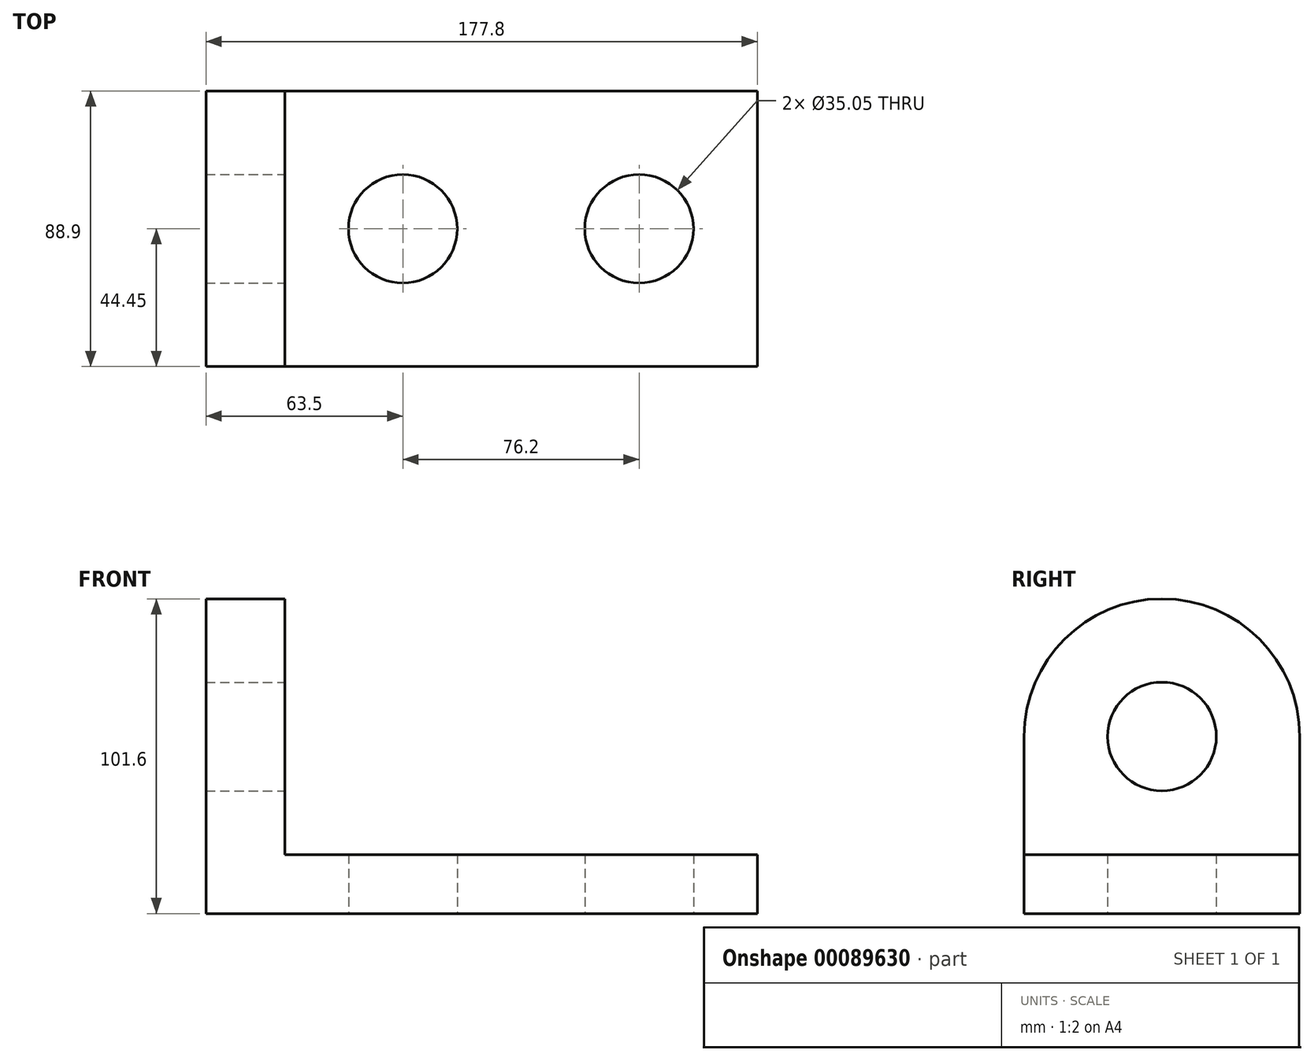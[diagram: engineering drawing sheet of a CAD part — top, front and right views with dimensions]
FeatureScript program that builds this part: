
annotation { "Feature Type Name" : "Feature", "Feature Type Description" : "" }
export const myFeature = defineFeature(function(context is Context, id is Id, definition is map)
    precondition{}
    {
        {
            var Q0;
            Q0=qCreatedBy(makeId("Top.planeOp"),FACE);
            var sketch = newSketch(context, id + "F0", { "sketchPlane" : qUnion([Q0])});
            skLineSegment(sketch, "E0.bottom", {"start": v(0, 0) * mm, "end": v(152.4, 0) * mm});
            skLineSegment(sketch, "E0.top", {"start": v(0, 88.9) * mm, "end": v(152.4, 88.9) * mm});
            skLineSegment(sketch, "E0.left", {"start": v(0, 0) * mm, "end": v(0, 88.9) * mm});
            skLineSegment(sketch, "E0.right", {"start": v(152.4, 0) * mm, "end": v(152.4, 88.9) * mm});
            skLineSegment(sketch, "E1", {"start": v(152.4, 44.45) * mm, "end": v(114.3, 44.45) * mm});
            skLineSegment(sketch, "E2", {"start": v(114.3, 44.45) * mm, "end": v(38.1, 44.45) * mm});
            skCircle(sketch, "E3", {"center": v(114.3, 44.45) * mm, "radius": 17.53 * mm});
            skCircle(sketch, "E4", {"center": v(38.1, 44.45) * mm, "radius": 26.9 * mm});
            skCircle(sketch, "E5", {"center": v(38.1, 44.45) * mm, "radius": 17.53 * mm});
            skSolve(sketch);
        }
        {
            var Q0;
            {var subQ1=sQuery(id+"F0.wireOp",EDGE,"E0.bottom");Q0=makeQuery(id+"F0.imprint","IMPRINT",FACE,{"disambiguationData":[TD([[makeQuery(id+"F0.imprint","IMPRINT",EDGE,{"derivedFrom":subQ1}),1.0]])]});}
            var Q1;
            Q1=makeQuery(id+"F0.imprint","IMPRINT",FACE,{"disambiguationData":[TD([[makeQuery(id+"F0.imprint","IMPRINT",EDGE,{"derivedFrom":sQuery(id+"F0.wireOp",EDGE,"E4")}),1.0]])]});
            extrude(context, id + "F1", {"entities" : qUnion([Q0, Q1]), "depth" : 19.05 * mm});
        }
        {
            var Q0;
            Q0=makeQuery(id+"F1.opExtrude","SWEPT_FACE",FACE,{"disambiguationData":[OSD([sQuery(id+"F0.wireOp",EDGE,"E0.left")])]});
            var sketch = newSketch(context, id + "F2", { "sketchPlane" : qUnion([Q0])});
            skLineSegment(sketch, "E6.bottom", {"start": v(0, 0) * mm, "end": v(-88.9, 0) * mm});
            skLineSegment(sketch, "E6.top", {"start": v(0, 57.15) * mm, "end": v(-88.9, 57.15) * mm});
            skLineSegment(sketch, "E6.left", {"start": v(0, 0) * mm, "end": v(0, 57.15) * mm});
            skLineSegment(sketch, "E6.right", {"start": v(-88.9, 0) * mm, "end": v(-88.9, 57.15) * mm});
            skCircle(sketch, "E7", {"center": v(-44.45, 57.15) * mm, "radius": 44.45 * mm});
            skCircle(sketch, "E8", {"center": v(-44.45, 57.15) * mm, "radius": 17.53 * mm});
            skSolve(sketch);
        }
        {
            var Q0;
            {var subQ1=sQuery(id+"F2.wireOp",EDGE,"E6.top");var subQ3=sQuery(id+"F2.wireOp",EDGE,"E8");var subQ4=makeQuery(id+"F2.imprint","INTERSECT",VERTEX,{"disambiguationData":[OD(0.0)],"derivedFrom":[subQ1,subQ3]});Q0=makeQuery(id+"F2.imprint","IMPRINT",FACE,{"disambiguationData":[TD([[makeQuery(id+"F2.imprint","IMPRINT",EDGE,{"disambiguationData":[TD([[subQ4,-1.0]])],"derivedFrom":subQ3}),-1.0]])]});}
            var Q1;
            {var subQ0=sQuery(id+"F2.wireOp",EDGE,"E6.left");var subQ1=makeQuery(id+"F1.opExtrude","CAP_EDGE",EDGE,{"disambiguationData":[OSD([sQuery(id+"F0.wireOp",EDGE,"E0.left")])],"isStart":false});var subQ2=makeQuery(id+"F2.imprint","INTERSECT",VERTEX,{"derivedFrom":[subQ1,subQ0]});Q1=makeQuery(id+"F2.imprint","IMPRINT",FACE,{"disambiguationData":[TD([[makeQuery(id+"F2.imprint","IMPRINT",EDGE,{"disambiguationData":[TD([[subQ2,-1.0]])],"derivedFrom":subQ1}),-1.0]])]});}
            var Q2;
            {var subQ0=sQuery(id+"F2.wireOp",EDGE,"E6.right");var subQ1=makeQuery(id+"F1.opExtrude","CAP_EDGE",EDGE,{"disambiguationData":[OSD([sQuery(id+"F0.wireOp",EDGE,"E0.left")])],"isStart":false});var subQ2=makeQuery(id+"F2.imprint","INTERSECT",VERTEX,{"derivedFrom":[subQ1,subQ0]});Q2=makeQuery(id+"F2.imprint","IMPRINT",FACE,{"disambiguationData":[TD([[makeQuery(id+"F2.imprint","IMPRINT",EDGE,{"disambiguationData":[TD([[subQ2,1.0]])],"derivedFrom":subQ1}),-1.0]])]});}
            var Q3;
            {var subQ0=sQuery(id+"F2.wireOp",EDGE,"E7");var subQ1=makeQuery(id+"F1.opExtrude","CAP_EDGE",EDGE,{"disambiguationData":[OSD([sQuery(id+"F0.wireOp",EDGE,"E0.left")])],"isStart":false});var subQ2=makeQuery(id+"F2.imprint","INTERSECT",VERTEX,{"disambiguationData":[OD(0.0)],"derivedFrom":[subQ1,subQ0]});Q3=makeQuery(id+"F2.imprint","IMPRINT",FACE,{"disambiguationData":[TD([[makeQuery(id+"F2.imprint","IMPRINT",EDGE,{"disambiguationData":[TD([[subQ2,-1.0]])],"derivedFrom":subQ0}),1.0]])]});}
            var Q4;
            {var subQ1=sQuery(id+"F2.wireOp",EDGE,"E6.bottom");Q4=makeQuery(id+"F2.imprint","IMPRINT",FACE,{"disambiguationData":[TD([[makeQuery(id+"F2.imprint","IMPRINT",EDGE,{"derivedFrom":subQ1}),-1.0]])]});}
            var Q5;
            {var subQ1=sQuery(id+"F2.wireOp",EDGE,"E6.top");var subQ7=sQuery(id+"F2.wireOp",EDGE,"E8");var subQ9=makeQuery(id+"F2.imprint","INTERSECT",VERTEX,{"disambiguationData":[OD(0.0)],"derivedFrom":[subQ1,subQ7]});Q5=makeQuery(id+"F2.imprint","IMPRINT",FACE,{"disambiguationData":[TD([[makeQuery(id+"F2.imprint","IMPRINT",EDGE,{"disambiguationData":[TD([[subQ9,1.0]])],"derivedFrom":subQ7}),-1.0]])]});}
            extrude(context, id + "F3", {"entities" : qUnion([Q0, Q1, Q2, Q3, Q4, Q5]), "operationType" : NewBodyOperationType.ADD, "depth" : 25.4 * mm});
        }
    });
